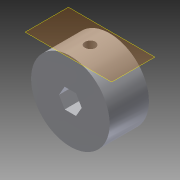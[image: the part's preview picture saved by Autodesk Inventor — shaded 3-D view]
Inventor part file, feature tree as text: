
AUTODESK INVENTOR PART (.ipt)
format: ipt  version: 2014 SP1 (Build 180222100, 222)  size: 105,472 bytes
history: native  units: in
note: dims shown in document units (in); Inventor stores cm internally (conversion verified against a paired STEP export)
features: extrude x3, sketch x3, plane x1
ambient origin geometry x8: Origin, YZ Plane, XZ Plane, XY Plane, X Axis, Y Axis, Z Axis, Center Point
bodies: Solid1 (feature_tree)
feature tree (7):
  extrude  "Extrusion1"  Depth=1.0in TaperAngle=0.0deg
  plane  "Work Plane1"
  extrude  "Extrusion2"  Depth=0.5in
  extrude  "Extrusion3"  Depth=0.5in
  sketch  "Sketch1"  dims[d0=2.0in d1=1.0in d2=0.0in]
  sketch  "Sketch2"  dims[d3=0.5in d4=0.266in]
  sketch  "Sketch3"  dims[d5=2.0in d6=0.0in d7=0.5in d8=2.0in d9=0.0in]
